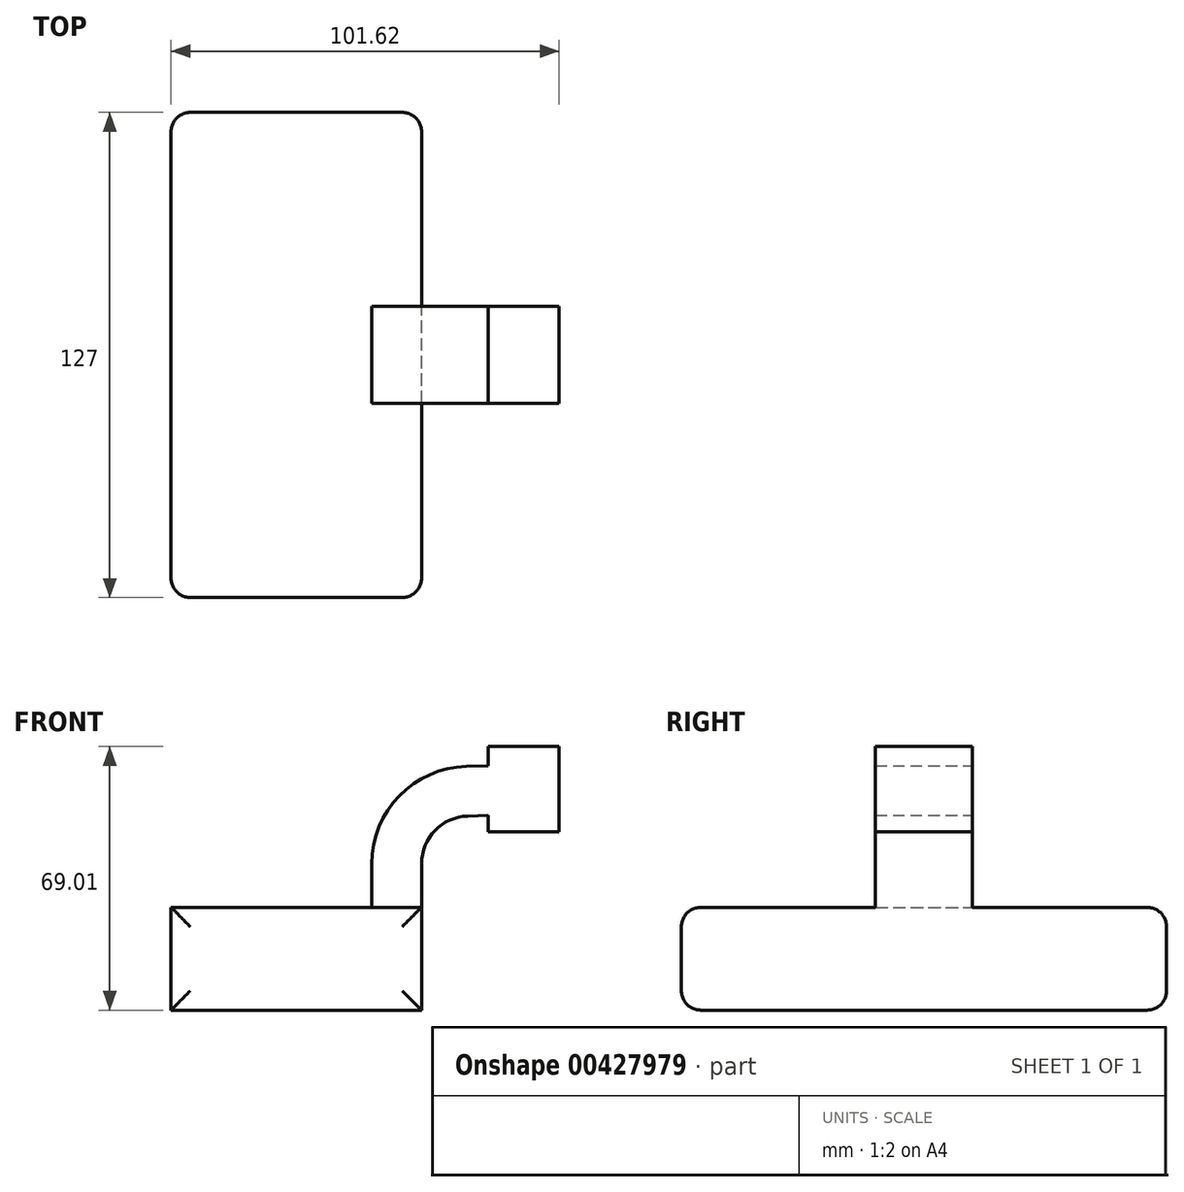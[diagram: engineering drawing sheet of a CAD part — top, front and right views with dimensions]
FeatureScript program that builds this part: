
annotation { "Feature Type Name" : "Feature", "Feature Type Description" : "" }
export const myFeature = defineFeature(function(context is Context, id is Id, definition is map)
    precondition{}
    {
        {
            var Q0;
            Q0=qCreatedBy(makeId("Front.planeOp"),FACE);
            var sketch = newSketch(context, id + "F0", { "sketchPlane" : qUnion([Q0])});
            skLineSegment(sketch, "E0.bottom", {"start": v(-32.8, 13.46) * mm, "end": v(32.8, 13.46) * mm});
            skLineSegment(sketch, "E0.top", {"start": v(-32.8, -13.46) * mm, "end": v(32.8, -13.46) * mm});
            skLineSegment(sketch, "E0.left", {"start": v(-32.8, 13.46) * mm, "end": v(-32.8, -13.46) * mm});
            skLineSegment(sketch, "E0.right", {"start": v(32.8, 13.46) * mm, "end": v(32.8, -13.46) * mm});
            skPoint(sketch, "E0.middle", {"position": v(0, 0) * mm});
            skLineSegment(sketch, "E1", {"start": v(32.8, 13.46) * mm, "end": v(32.8, 24.84) * mm});
            skArc(sketch, "E2", {"start": v(32.8, 24.84) * mm, "mid": v(36.33, 33.55) * mm, "end": v(44.93, 37.35) * mm});
            skLineSegment(sketch, "E3", {"start": v(44.93, 37.35) * mm, "end": v(59.93, 37.81) * mm});
            skLineSegment(sketch, "E4.0", {"start": v(44.53, 50.37) * mm, "end": v(59.53, 50.83) * mm});
            skArc(sketch, "E4.1", {"start": v(19.77, 24.84) * mm, "mid": v(26.98, 42.62) * mm, "end": v(44.53, 50.37) * mm});
            skLineSegment(sketch, "E4.2", {"start": v(19.77, 13.46) * mm, "end": v(19.77, 24.84) * mm});
            skLineSegment(sketch, "E5.bottom", {"start": v(50.24, 55.55) * mm, "end": v(68.82, 55.55) * mm});
            skLineSegment(sketch, "E5.top", {"start": v(50.24, 33.18) * mm, "end": v(68.82, 33.18) * mm});
            skLineSegment(sketch, "E5.left", {"start": v(50.24, 55.55) * mm, "end": v(50.24, 33.18) * mm});
            skLineSegment(sketch, "E5.right", {"start": v(68.82, 55.55) * mm, "end": v(68.82, 33.18) * mm});
            skPoint(sketch, "E5.middle", {"position": v(59.53, 44.37) * mm});
            skLineSegment(sketch, "E6", {"start": v(59.53, 55.55) * mm, "end": v(59.93, 33.18) * mm});
            skPoint(sketch, "E6.startSnap0", {"position": v(59.53, 55.55) * mm});
            skSolve(sketch);
        }
        {
            var Q0;
            Q0=makeQuery(id+"F0.imprint","IMPRINT",FACE,{"disambiguationData":[TD([[makeQuery(id+"F0.imprint","IMPRINT",EDGE,{"derivedFrom":sQuery(id+"F0.wireOp",EDGE,"E0.top")}),1.0]])]});
            extrude(context, id + "F1", {"entities" : qUnion([Q0]), "endBound" : BoundingType.SYMMETRIC, "depth" : 127 * mm});
        }
        {
            var Q0;
            {var subQ4=sQuery(id+"F0.wireOp",EDGE,"E1");Q0=makeQuery(id+"F0.imprint","IMPRINT",FACE,{"disambiguationData":[TD([[makeQuery(id+"F0.imprint","IMPRINT",EDGE,{"derivedFrom":subQ4}),1.0]])]});}
            var Q1;
            {var subQ0=sQuery(id+"F0.wireOp",EDGE,"E5.left");var subQ1=sQuery(id+"F0.wireOp",EDGE,"E3");var subQ2=makeQuery(id+"F0.imprint","INTERSECT",VERTEX,{"derivedFrom":[subQ1,subQ0]});Q1=makeQuery(id+"F0.imprint","IMPRINT",FACE,{"disambiguationData":[TD([[makeQuery(id+"F0.imprint","IMPRINT",EDGE,{"disambiguationData":[TD([[subQ2,-1.0]])],"derivedFrom":subQ1}),-1.0]])]});}
            var Q2;
            {var subQ0=sQuery(id+"F0.wireOp",EDGE,"E5.right");Q2=makeQuery(id+"F0.imprint","IMPRINT",FACE,{"disambiguationData":[TD([[makeQuery(id+"F0.imprint","IMPRINT",EDGE,{"derivedFrom":subQ0}),-1.0]])]});}
            var Q3;
            {var subQ0=sQuery(id+"F0.wireOp",EDGE,"E5.left");var subQ4=sQuery(id+"F0.wireOp",EDGE,"E3");var subQ5=makeQuery(id+"F0.imprint","INTERSECT",VERTEX,{"derivedFrom":[subQ4,subQ0]});Q3=makeQuery(id+"F0.imprint","IMPRINT",FACE,{"disambiguationData":[TD([[makeQuery(id+"F0.imprint","IMPRINT",EDGE,{"disambiguationData":[TD([[subQ5,-1.0]])],"derivedFrom":subQ4}),1.0]])]});}
            extrude(context, id + "F2", {"entities" : qUnion([Q0, Q1, Q2, Q3]), "operationType" : NewBodyOperationType.ADD, "endBound" : BoundingType.SYMMETRIC, "depth" : 25.4 * mm});
        }
        {
            var Q0;
            Q0=makeQuery(id+"F1.opExtrude","CAP_FACE",FACE,{"disambiguationData":[OSD([sQuery(id+"F0.wireOp",EDGE,"E0.bottom"),sQuery(id+"F0.wireOp",EDGE,"E0.top"),sQuery(id+"F0.wireOp",EDGE,"E0.left"),sQuery(id+"F0.wireOp",EDGE,"E0.right")])],"isStart":false});
            var Q1;
            Q1=makeQuery(id+"F1.opExtrude","CAP_FACE",FACE,{"disambiguationData":[OSD([sQuery(id+"F0.wireOp",EDGE,"E0.bottom"),sQuery(id+"F0.wireOp",EDGE,"E0.top"),sQuery(id+"F0.wireOp",EDGE,"E0.left"),sQuery(id+"F0.wireOp",EDGE,"E0.right")])],"isStart":true});
            fillet(context, id + "F3", {"entities" : qUnion([Q0, Q1]), "radius" : 5.08 * mm, "tangentPropagation" : true, "allowEdgeOverflow" : false});
        }
    });
